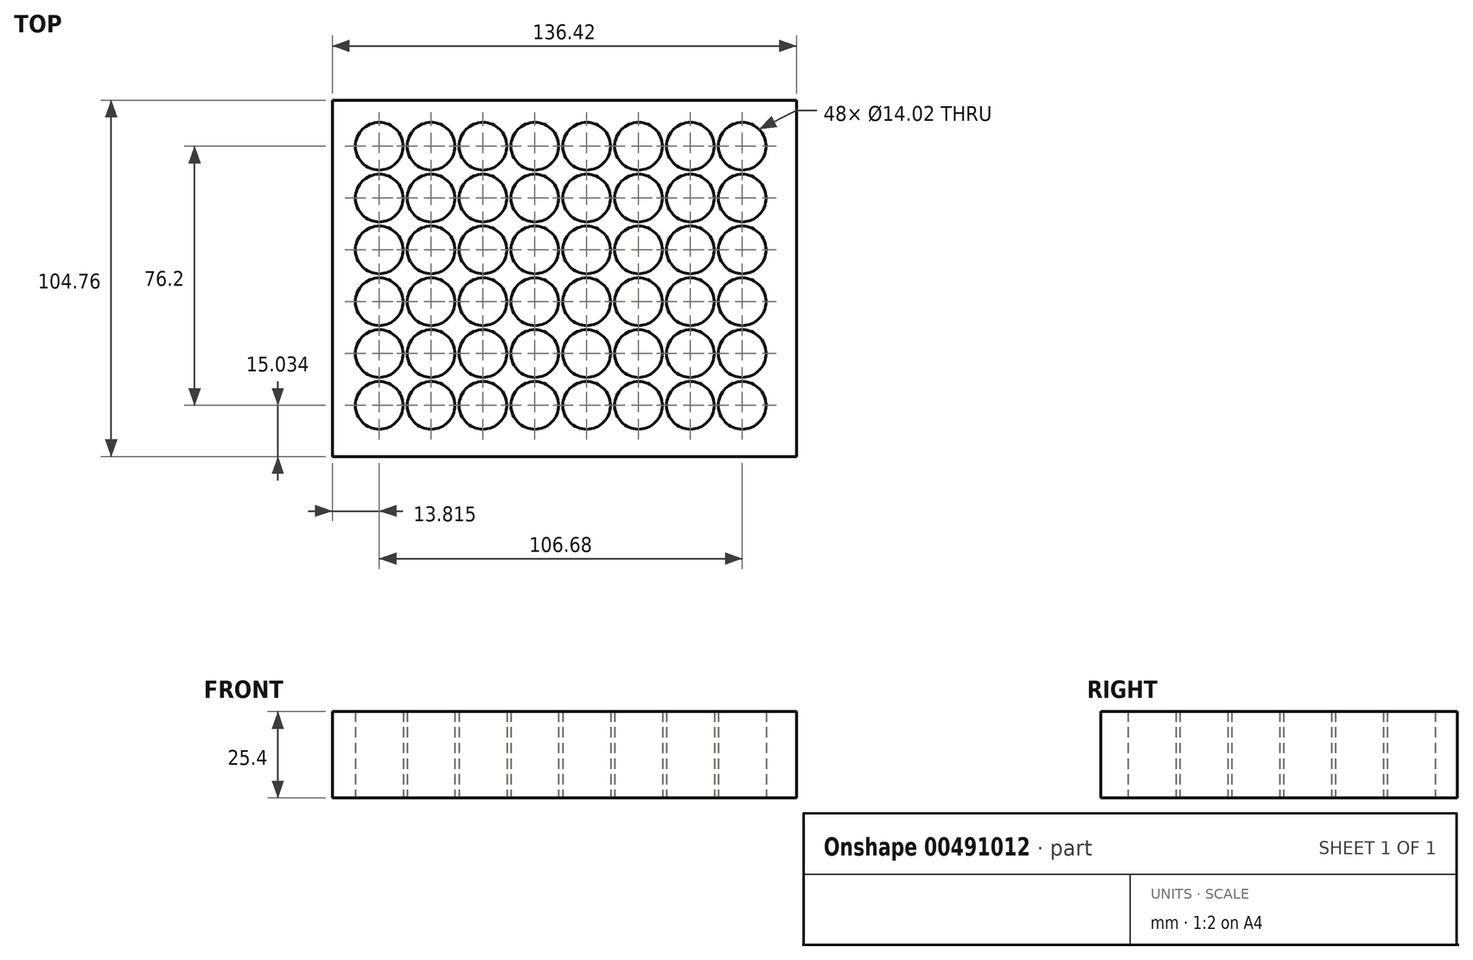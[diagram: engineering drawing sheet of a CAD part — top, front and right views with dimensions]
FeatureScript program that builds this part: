
annotation { "Feature Type Name" : "Feature", "Feature Type Description" : "" }
export const myFeature = defineFeature(function(context is Context, id is Id, definition is map)
    precondition{}
    {
        {
            var Q0;
            Q0=qCreatedBy(makeId("Top.planeOp"),FACE);
            var sketch = newSketch(context, id + "F0", { "sketchPlane" : qUnion([Q0])});
            skLineSegment(sketch, "E0.bottom", {"start": v(68.2, 52.38) * mm, "end": v(-68.2, 52.38) * mm});
            skLineSegment(sketch, "E0.top", {"start": v(68.2, -52.38) * mm, "end": v(-68.2, -52.38) * mm});
            skLineSegment(sketch, "E0.left", {"start": v(68.2, 52.38) * mm, "end": v(68.2, -52.38) * mm});
            skLineSegment(sketch, "E0.right", {"start": v(-68.2, 52.38) * mm, "end": v(-68.2, -52.38) * mm});
            skPoint(sketch, "E0.middle", {"position": v(0, 0) * mm});
            skCircle(sketch, "E1", {"center": v(-54.4, 38.85) * mm, "radius": 7 * mm});
            skCircle(sketch, "E2.0.1.0", {"center": v(-54.4, 23.61) * mm, "radius": 7 * mm});
            skCircle(sketch, "E2.0.2.0", {"center": v(-54.4, 8.37) * mm, "radius": 7 * mm});
            skCircle(sketch, "E2.0.3.0", {"center": v(-54.4, -6.87) * mm, "radius": 7 * mm});
            skCircle(sketch, "E2.0.4.0", {"center": v(-54.4, -22.1) * mm, "radius": 7 * mm});
            skCircle(sketch, "E2.0.5.0", {"center": v(-54.4, -37.35) * mm, "radius": 7 * mm});
            skCircle(sketch, "E2.1.0.0", {"center": v(-39.16, 38.85) * mm, "radius": 7 * mm});
            skCircle(sketch, "E2.1.1.0", {"center": v(-39.16, 23.61) * mm, "radius": 7 * mm});
            skCircle(sketch, "E2.1.2.0", {"center": v(-39.16, 8.37) * mm, "radius": 7 * mm});
            skCircle(sketch, "E2.1.3.0", {"center": v(-39.16, -6.87) * mm, "radius": 7 * mm});
            skCircle(sketch, "E2.1.4.0", {"center": v(-39.16, -22.1) * mm, "radius": 7 * mm});
            skCircle(sketch, "E2.1.5.0", {"center": v(-39.16, -37.35) * mm, "radius": 7 * mm});
            skCircle(sketch, "E2.2.0.0", {"center": v(-23.92, 38.85) * mm, "radius": 7 * mm});
            skCircle(sketch, "E2.2.1.0", {"center": v(-23.92, 23.61) * mm, "radius": 7 * mm});
            skCircle(sketch, "E2.2.2.0", {"center": v(-23.92, 8.37) * mm, "radius": 7 * mm});
            skCircle(sketch, "E2.2.3.0", {"center": v(-23.92, -6.87) * mm, "radius": 7 * mm});
            skCircle(sketch, "E2.2.4.0", {"center": v(-23.92, -22.1) * mm, "radius": 7 * mm});
            skCircle(sketch, "E2.2.5.0", {"center": v(-23.92, -37.35) * mm, "radius": 7 * mm});
            skCircle(sketch, "E2.3.0.0", {"center": v(-8.68, 38.85) * mm, "radius": 7 * mm});
            skCircle(sketch, "E2.3.1.0", {"center": v(-8.68, 23.61) * mm, "radius": 7 * mm});
            skCircle(sketch, "E2.3.2.0", {"center": v(-8.68, 8.37) * mm, "radius": 7 * mm});
            skCircle(sketch, "E2.3.3.0", {"center": v(-8.68, -6.87) * mm, "radius": 7 * mm});
            skCircle(sketch, "E2.3.4.0", {"center": v(-8.68, -22.1) * mm, "radius": 7 * mm});
            skCircle(sketch, "E2.3.5.0", {"center": v(-8.68, -37.35) * mm, "radius": 7 * mm});
            skCircle(sketch, "E2.4.0.0", {"center": v(6.56, 38.85) * mm, "radius": 7 * mm});
            skCircle(sketch, "E2.4.1.0", {"center": v(6.56, 23.61) * mm, "radius": 7 * mm});
            skCircle(sketch, "E2.4.2.0", {"center": v(6.56, 8.37) * mm, "radius": 7 * mm});
            skCircle(sketch, "E2.4.3.0", {"center": v(6.56, -6.87) * mm, "radius": 7 * mm});
            skCircle(sketch, "E2.4.4.0", {"center": v(6.56, -22.1) * mm, "radius": 7 * mm});
            skCircle(sketch, "E2.4.5.0", {"center": v(6.56, -37.35) * mm, "radius": 7 * mm});
            skCircle(sketch, "E2.5.0.0", {"center": v(21.8, 38.85) * mm, "radius": 7 * mm});
            skCircle(sketch, "E2.5.1.0", {"center": v(21.8, 23.61) * mm, "radius": 7 * mm});
            skCircle(sketch, "E2.5.2.0", {"center": v(21.8, 8.37) * mm, "radius": 7 * mm});
            skCircle(sketch, "E2.5.3.0", {"center": v(21.8, -6.87) * mm, "radius": 7 * mm});
            skCircle(sketch, "E2.5.4.0", {"center": v(21.8, -22.1) * mm, "radius": 7 * mm});
            skCircle(sketch, "E2.5.5.0", {"center": v(21.8, -37.35) * mm, "radius": 7 * mm});
            skCircle(sketch, "E2.6.0.0", {"center": v(37.04, 38.85) * mm, "radius": 7 * mm});
            skCircle(sketch, "E2.6.1.0", {"center": v(37.04, 23.61) * mm, "radius": 7 * mm});
            skCircle(sketch, "E2.6.2.0", {"center": v(37.04, 8.37) * mm, "radius": 7 * mm});
            skCircle(sketch, "E2.6.3.0", {"center": v(37.04, -6.87) * mm, "radius": 7 * mm});
            skCircle(sketch, "E2.6.4.0", {"center": v(37.04, -22.1) * mm, "radius": 7 * mm});
            skCircle(sketch, "E2.6.5.0", {"center": v(37.04, -37.35) * mm, "radius": 7 * mm});
            skCircle(sketch, "E2.7.0.0", {"center": v(52.28, 38.85) * mm, "radius": 7 * mm});
            skCircle(sketch, "E2.7.1.0", {"center": v(52.28, 23.61) * mm, "radius": 7 * mm});
            skCircle(sketch, "E2.7.2.0", {"center": v(52.28, 8.37) * mm, "radius": 7 * mm});
            skCircle(sketch, "E2.7.3.0", {"center": v(52.28, -6.87) * mm, "radius": 7 * mm});
            skCircle(sketch, "E2.7.4.0", {"center": v(52.28, -22.1) * mm, "radius": 7 * mm});
            skCircle(sketch, "E2.7.5.0", {"center": v(52.28, -37.35) * mm, "radius": 7 * mm});
            skLineSegment(sketch, "E2.direction1", {"start": v(-54.4, 38.85) * mm, "end": v(-39.16, 38.85) * mm, "construction": true});
            skLineSegment(sketch, "E2.direction2", {"start": v(-54.4, 38.85) * mm, "end": v(-54.4, 23.61) * mm, "construction": true});
            skSolve(sketch);
        }
        {
            var Q0;
            Q0 = qSketchRegion(id + "F0", true);
            extrude(context, id + "F1", {"entities" : qUnion([Q0]), "depth" : 25.4 * mm});
        }
    });
